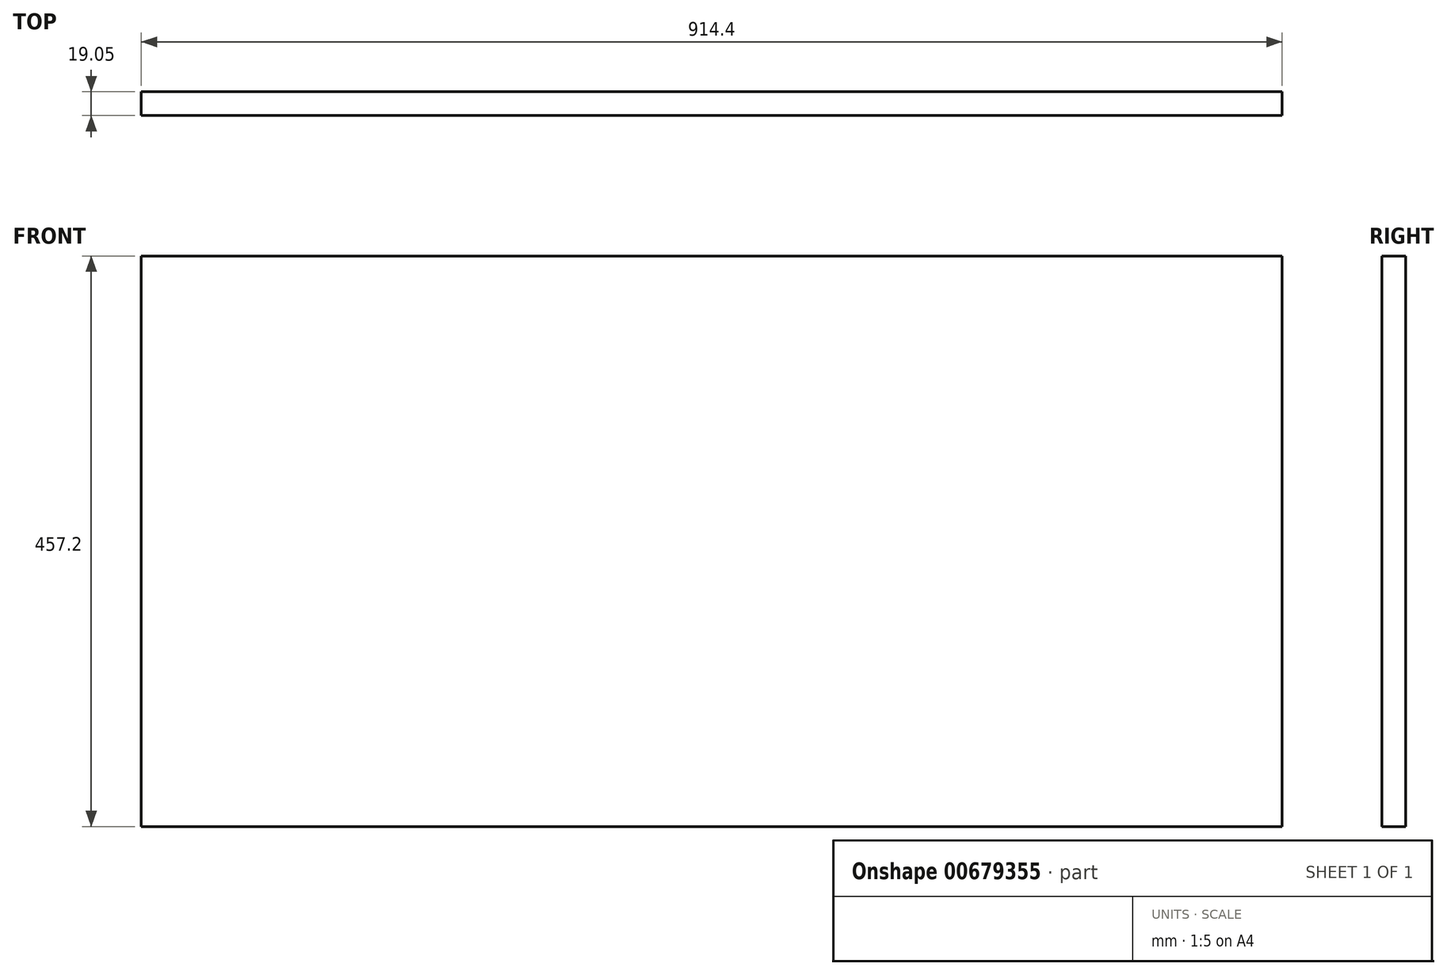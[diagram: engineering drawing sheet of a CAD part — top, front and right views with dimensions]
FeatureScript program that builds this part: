
annotation { "Feature Type Name" : "Feature", "Feature Type Description" : "" }
export const myFeature = defineFeature(function(context is Context, id is Id, definition is map)
    precondition{}
    {
        {
            var Q0;
            Q0=qCreatedBy(makeId("Front.planeOp"),FACE);
            var sketch = newSketch(context, id + "F0", { "sketchPlane" : qUnion([Q0])});
            skLineSegment(sketch, "E0.bottom", {"start": v(-457.2, 228.6) * mm, "end": v(457.2, 228.6) * mm});
            skLineSegment(sketch, "E0.top", {"start": v(-457.2, -228.6) * mm, "end": v(457.2, -228.6) * mm});
            skLineSegment(sketch, "E0.left", {"start": v(-457.2, 228.6) * mm, "end": v(-457.2, -228.6) * mm});
            skLineSegment(sketch, "E0.right", {"start": v(457.2, 228.6) * mm, "end": v(457.2, -228.6) * mm});
            skPoint(sketch, "E0.middle", {"position": v(0, 0) * mm});
            skSolve(sketch);
        }
        {
            var Q0;
            Q0=makeQuery(id+"F0.imprint","IMPRINT",FACE,{"disambiguationData":[TD([[makeQuery(id+"F0.imprint","IMPRINT",EDGE,{"derivedFrom":sQuery(id+"F0.wireOp",EDGE,"E0.bottom")}),-1.0]])]});
            extrude(context, id + "F1", {"entities" : qUnion([Q0]), "depth" : 19.05 * mm, "offsetDistance" : 25.4 * mm});
        }
    });
